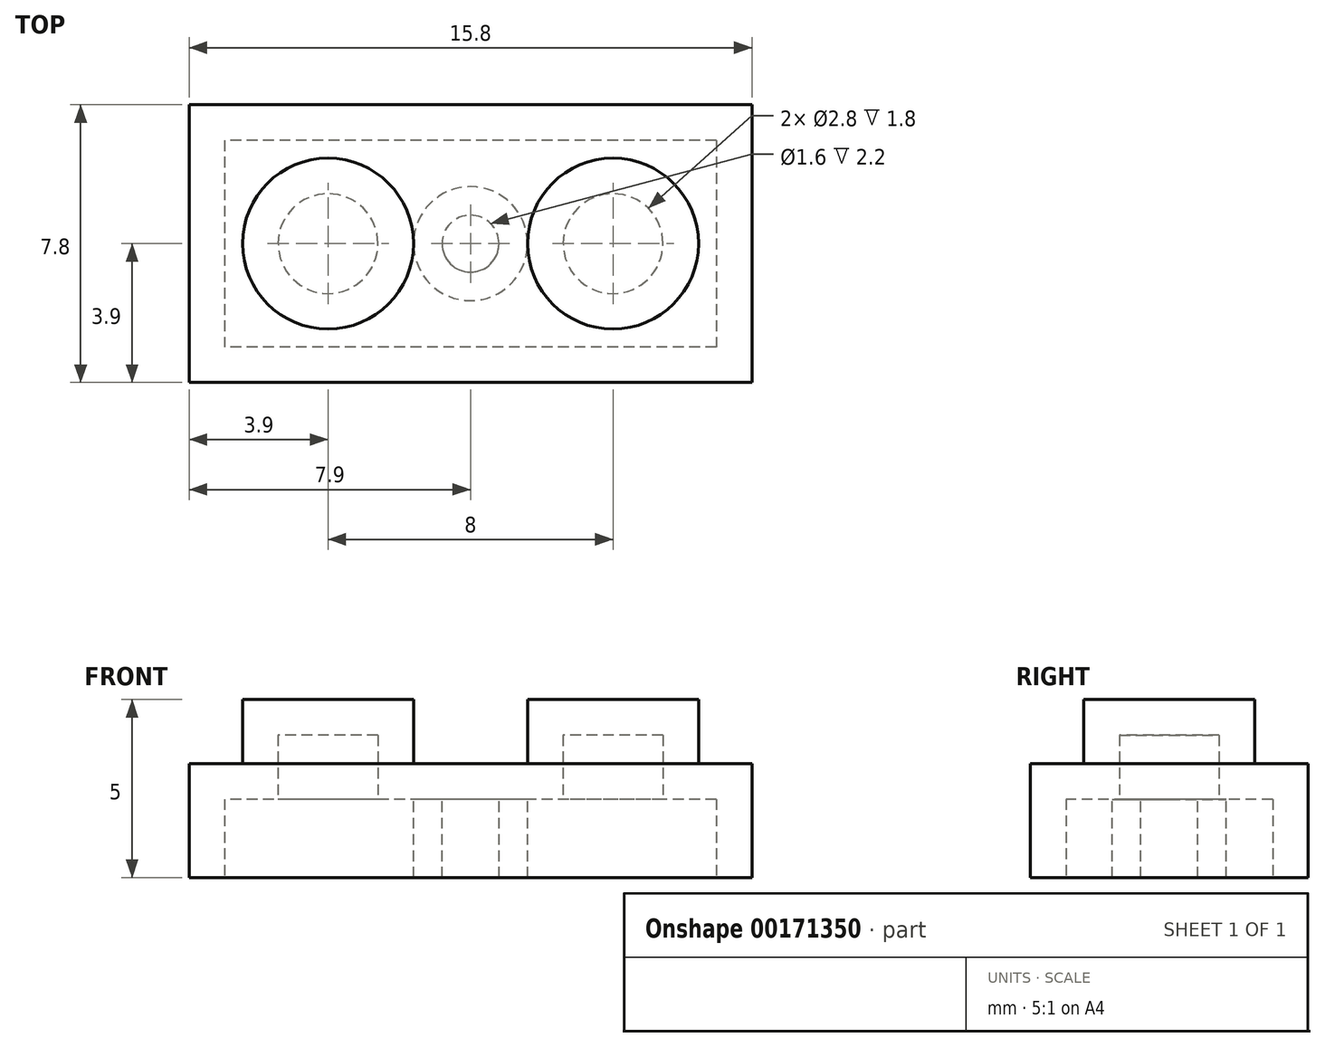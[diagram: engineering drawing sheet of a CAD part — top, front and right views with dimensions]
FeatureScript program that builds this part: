
annotation { "Feature Type Name" : "Feature", "Feature Type Description" : "" }
export const myFeature = defineFeature(function(context is Context, id is Id, definition is map)
    precondition{}
    {
        {
            var Q0;
            Q0=qCreatedBy(makeId("Top.planeOp"),FACE);
            var sketch = newSketch(context, id + "F0", { "sketchPlane" : qUnion([Q0])});
            skLineSegment(sketch, "E0.bottom", {"start": v(7.9, 3.9) * mm, "end": v(-7.9, 3.9) * mm});
            skLineSegment(sketch, "E0.top", {"start": v(7.9, -3.9) * mm, "end": v(-7.9, -3.9) * mm});
            skLineSegment(sketch, "E0.left", {"start": v(7.9, 3.9) * mm, "end": v(7.9, -3.9) * mm});
            skLineSegment(sketch, "E0.right", {"start": v(-7.9, 3.9) * mm, "end": v(-7.9, -3.9) * mm});
            skPoint(sketch, "E0.middle", {"position": v(0, 0) * mm});
            skSolve(sketch);
        }
        {
            var Q0;
            Q0 = qSketchRegion(id + "F0", true);
            extrude(context, id + "F1", {"entities" : qUnion([Q0]), "depth" : 3.2 * mm});
        }
        {
            var Q0;
            Q0=makeQuery(id+"F1.opExtrude","CAP_FACE",FACE,{"disambiguationData":[OSD([sQuery(id+"F0.wireOp",EDGE,"E0.bottom"),sQuery(id+"F0.wireOp",EDGE,"E0.top"),sQuery(id+"F0.wireOp",EDGE,"E0.left"),sQuery(id+"F0.wireOp",EDGE,"E0.right")])],"isStart":false});
            var sketch = newSketch(context, id + "F2", { "sketchPlane" : qUnion([Q0])});
            skCircle(sketch, "E1", {"center": v(-4, 0) * mm, "radius": 2.4 * mm});
            skCircle(sketch, "E2", {"center": v(4, 0) * mm, "radius": 2.4 * mm});
            skLineSegment(sketch, "E3", {"start": v(4, 0) * mm, "end": v(-4, 0) * mm, "construction": true});
            skPoint(sketch, "E4", {"position": v(-6.4, 0) * mm});
            skSolve(sketch);
        }
        {
            var Q0;
            Q0 = qSketchRegion(id + "F2", true);
            extrude(context, id + "F3", {"entities" : qUnion([Q0]), "operationType" : NewBodyOperationType.ADD, "depth" : 1.8 * mm});
        }
        {
            var Q0;
            Q0=makeQuery(id+"F1.opExtrude","CAP_FACE",FACE,{"disambiguationData":[OSD([sQuery(id+"F0.wireOp",EDGE,"E0.bottom"),sQuery(id+"F0.wireOp",EDGE,"E0.top"),sQuery(id+"F0.wireOp",EDGE,"E0.left"),sQuery(id+"F0.wireOp",EDGE,"E0.right")])],"isStart":true});
            shell(context, id + "F4", {"entities" : qUnion([Q0]), "thickness" : 1 * mm});
        }
        {
            var Q0;
            Q0=makeQuery(id+"F4.opShell","OFFSET_FACE",FACE,{"disambiguationData":[OSD([sQuery(id+"F0.wireOp",EDGE,"E0.bottom"),sQuery(id+"F0.wireOp",EDGE,"E0.top"),sQuery(id+"F0.wireOp",EDGE,"E0.left"),sQuery(id+"F0.wireOp",EDGE,"E0.right")])]});
            var sketch = newSketch(context, id + "F5", { "sketchPlane" : qUnion([Q0])});
            skCircle(sketch, "E5", {"center": v(0, 0) * mm, "radius": 0.8 * mm});
            skCircle(sketch, "E6", {"center": v(0, 0) * mm, "radius": 1.6 * mm});
            skSolve(sketch);
        }
        {
            var Q0;
            Q0 = qSketchRegion(id + "F5", true);
            var Q1;
            Q1=makeQuery(id+"F1.opExtrude","CAP_FACE",FACE,{"disambiguationData":[OSD([sQuery(id+"F0.wireOp",EDGE,"E0.bottom"),sQuery(id+"F0.wireOp",EDGE,"E0.top"),sQuery(id+"F0.wireOp",EDGE,"E0.left"),sQuery(id+"F0.wireOp",EDGE,"E0.right")])],"isStart":true});
            extrude(context, id + "F6", {"entities" : qUnion([Q0]), "operationType" : NewBodyOperationType.ADD, "endBound" : BoundingType.UP_TO_SURFACE, "endBoundEntityFace" : qUnion([Q1]), "depth" : 25 * mm});
        }
    });
